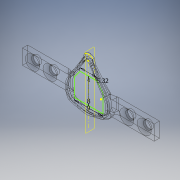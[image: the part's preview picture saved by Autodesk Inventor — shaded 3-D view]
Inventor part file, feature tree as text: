
AUTODESK INVENTOR PART (.ipt)
format: ipt  version: 2018 (Build 220112000, 112)  size: 948,736 bytes
history: native  units: mm
features: sketch x35, extrude x29, fillet x12, plane x2, mirror x2, hole x1, direct_edit x1, other x1
ambient origin geometry x8: Origin, YZ Plane, XZ Plane, XY Plane, X Axis, Y Axis, Z Axis, Center Point
bodies: Solid1 (feature_tree)
feature tree (83):
  extrude  "Extrusion1"  Depth=7.5mm TaperAngle=0.0deg
  extrude  "Extrusion2"  Depth=40.0mm TaperAngle=0.0deg
  extrude  "Extrusion6"  Depth=40.0mm TaperAngle=0.0deg
  extrude  "Extrusion7"  Depth=0.6mm TaperAngle=0.0deg
  extrude  "Extrusion9"  Depth=8.0mm
  extrude  "Extrusion10"  Depth=10.0mm TaperAngle=0.0deg
  sketch  "Sketch17"  dims[d90=10.0mm d91=0.0mm d92=10.0mm d93=0.0mm]
  sketch  "Sketch21"  dims[d96=7.389394mm d99=3.467mm]
  extrude  "Extrusion12"  Depth=3.467mm
  extrude  "Extrusion13"  Depth=2.2mm
  extrude  "Extrusion14"  Depth=3.467mm
  extrude  "Extrusion15"  Depth=16.015mm
  sketch  "Sketch28"  dims[d126=4.0mm d127=23.35mm]
  extrude  "Extrusion16"  Depth=4.0mm
  hole  "Hole6"  [1 undecoded]
  sketch  "Sketch31"  dims[d129=3.467mm d130=4.369mm d131=5.824mm d132=2.0mm d133=14.3117mm d134=6.637mm d135=20.594885mm d136=10.0mm d137=0.0mm]
  extrude  "Extrusion18"  Depth=10.0mm TaperAngle=0.0deg
  direct_edit  "Direct Edit1"
  extrude  "Extrusion19"  Depth=10.0mm
  extrude  "Extrusion20"  Depth=0.066mm
  extrude  "Extrusion21"  TaperAngle=0.0deg  [1 undecoded]
  extrude  "Extrusion22"  Depth=0.066mm
  extrude  "Extrusion23"  Depth=10.0mm TaperAngle=0.0deg
  sketch  "Sketch38"  dims[d167=8.0mm d168=0.0mm d169=0.0mm]
  extrude  "Extrusion24"  Depth=5.320111mm
  extrude  "Extrusion25"  TaperAngle=0.0deg  [1 undecoded]
  extrude  "Extrusion26"  Depth=10.0mm TaperAngle=0.0deg
  sketch  "Sketch42"  dims[d181=0.0mm d182=0.0mm d183=0.67mm d184=0.0mm]
  plane  "Work Plane1"
  mirror  "Mirror7"
  sketch  "Sketch43"  dims[d185=0.67mm d186=0.0mm d187=2.0mm]
  extrude  "Extrusion27"  Depth=1.128mm TaperAngle=0.0deg
  extrude  "Extrusion28"  TaperAngle=0.0deg  [1 undecoded]
  extrude  "Extrusion29"  Depth=0.67mm TaperAngle=0.0deg
  extrude  "Extrusion30"  Depth=2.0mm
  extrude  "Extrusion31"  Depth=2.0mm
  mirror  "Mirror8"
  extrude  "Extrusion32"  Depth=2.0mm TaperAngle=0.0deg
  fillet  "Fillet3"  Radius=2.0mm
  fillet  "Fillet4"  Radius=0.518mm
  fillet  "Fillet5"  [1 undecoded]
  fillet  "Fillet6"  Radius=0.67mm
  extrude  "Extrusion33"  Depth=2.0mm
  fillet  "Fillet7"  Radius=2.0mm
  fillet  "Fillet8"  Radius=0.843mm
  extrude  "Extrusion34"  Depth=2.0mm
  extrude  "Extrusion35"  Depth=1.0mm
  fillet  "Fillet9"  [1 undecoded]
  fillet  "Fillet10"  [1 undecoded]
  fillet  "Fillet11"  [1 undecoded]
  fillet  "Fillet12"  [1 undecoded]
  fillet  "Fillet13"  [1 undecoded]
  fillet  "Fillet14"  [1 undecoded]
  sketch  "Sketch1"  dims[d0=7.5mm d1=22.5mm d2=1.25mm d3=0.0mm d4=6.5mm d5=18.5mm d6=1.15mm d7=0.0mm]
  sketch  "Sketch3"  dims[d36=40.0mm d37=0.0mm d38=40.0mm d39=0.0mm]
  sketch  "Sketch10"  dims[d43=55.0mm d44=0.0mm d45=40.0mm d46=0.0mm]
  sketch  "Sketch11"  dims[d80=0.9mm d81=0.0mm d82=0.6mm d83=0.0mm]
  sketch  "Sketch16"  dims[d84=0.6mm d85=0.0mm d86=8.0mm]
  sketch  "Sketch22"  dims[d100=3.467mm d114=2.2mm]
  sketch  "Sketch24"  dims[d117=3.467mm d118=3.467mm]
  sketch  "Sketch25"  dims[d120=16.015mm d121=16.015mm]
  sketch  "Sketch27"  dims[d124=4.0mm d125=4.0mm]
  sketch  "Sketch29"  dims[d128=23.35mm]
  sketch  "Sketch32"  dims[d138=7.5mm d139=10.0mm d140=10.0mm d141=46.7mm]
  sketch  "Sketch33"  dims[d146=0.0mm d147=0.0mm d151=0.066mm]
  sketch  "Sketch34"  dims[d152=0.0mm d153=0.0mm d154=0.0mm d155=0.0mm]
  sketch  "Sketch35"  dims[d156=0.066mm d157=0.066mm]
  sketch  "Sketch36"  dims[d158=10.0mm d159=0.0mm d160=10.0mm d161=0.0mm]
  sketch  "Sketch37"  dims[d162=9.0mm d166=5.320111mm]
  sketch  "Sketch39"  dims[d170=10.0mm d171=0.0mm d172=1.128mm d173=0.0mm]
  sketch  "Sketch40"  dims[d174=-3.98mm d175=1.128mm d176=0.0mm]
  sketch  "Sketch41"  dims[d177=0.67mm d178=0.0mm d179=0.0mm d180=0.0mm]
  sketch  "Sketch44"  dims[d188=2.0mm d189=2.0mm]
  sketch  "Sketch45"  dims[d190=2.0mm d191=0.67mm d192=0.0mm d193=2.0mm d194=0.518mm d195=0.0mm d196=0.0mm d197=0.67mm d198=0.0mm]
  sketch  "Sketch46"  dims[d199=2.0mm d200=2.0mm d201=2.0mm d202=0.843mm]
  sketch  "Sketch47"  dims[d203=2.0mm d204=2.0mm]
  sketch  "Sketch48"  dims[d21=1.0mm d22=1.0mm]
  plane  "Work Plane2"
  sketch  "Sketch49"
  sketch  "Sketch50"
  sketch  "Sketch51"
  sketch  "Sketch52"
  other  "Scale1"
note: 11 required parameter values undecoded (feature->parameter linkage not recoverable at this tier; creation-order binding heuristic only, values carry confidence <= 0.55)
